# Revit family: Planting_-_Solid_and_RPC_16077
name_source: partatom
category: Planting
revit_build: Autodesk Revit Architecture 2015 (Build: 20140322_1515(x64)
units: mm (PartAtom-declared; Revit-internal decimal feet)

## types (15) — shared parameters
Assembly Code = G2050500
Planting Profile Material = <By Category>

## per-type parameters (varying)
| type | Canopy Height | Canopy Ratio | Form | Height | Reference Plane Height | Truck Width | Width |
| Deciduous - Med - Ash | 28' - 8 13/32" | 0.82 | Solids : Round Upright | 35' - 0" | 17' - 6" | 1' - 8" | 25' - 0" |
| Deciduous - Large - Oak, Skinny | 42' - 0" | 0.84 | Solids : Round | 50' - 0" | 25' - 0" | 2' - 8" | 40' - 0" |
| Deciduous - Large - Oak, Wide | 46' - 2 13/32" | 0.84 | Solids : Round | 55' - 0" | 27' - 6" | 3' - 1 19/32" | 47' - 0" |
| Deciduous - Med - Honey Locust | 34' - 4 13/16" | 0.86 | Solids : Vase | 40' - 0" | 20' - 0" | 1' - 8" | 25' - 0" |
| Deciduous - Large - Beech | 37' - 4 3/16" | 0.83 | Solids : Round | 45' - 0" | 22' - 6" | 2' - 3 3/16" | 34' - 0" |
| Deciduous - Small - Serviceberry | 22' - 6" | 0.9 | Solids : Round | 25' - 0" | 12' - 6" | 1' - 0" | 15' - 0" |
| Deciduous - Med - Birch | 27' - 0" | 0.9 | Solids : Round Upright | 30' - 0" | 15' - 0" | 1' - 0" | 15' - 0" |
| Evergreen - Juniper, Wide | 24' - 6" | 0.98 | Solids : Columnar | 25' - 0" | 12' - 6" | 0' - 8" | 10' - 0" |
| Evergreen - Juniper, Skinny | 34' - 3 19/32" | 0.98 | Solids : Columnar | 35' - 0" | 17' - 6" | 0' - 6 13/32" | 8' - 0" |
| Evergreen - Fir | 31' - 6" | 0.9 | Solids : Conical | 35' - 0" | 17' - 6" | 1' - 4" | 20' - 0" |
| Evergreen - Hemlock | 33' - 3" | 0.95 | Solids : Pyramidal | 35' - 0" | 17' - 6" | 1' - 2 13/32" | 18' - 0" |
| Evergreen - Spruce | 42' - 3 19/32" | 0.94 | Solids : Conical | 45' - 0" | 22' - 6" | 1' - 4" | 20' - 0" |
| Deciduous - Small - Blueberry | 20' - 0" | 0.8 | Solids : Vase | 25' - 0" | 12' - 6" | 1' - 8" | 25' - 0" |
| Deciduous - Small - Cherry | 24' - 7 3/16" | 0.82 | Solids : Vase | 30' - 0" | 15' - 0" | 1' - 2 13/32" | 18' - 0" |
| Deciduous - Small - Apple | 24' - 0" | 0.8 | Solids : Vase | 30' - 0" | 15' - 0" | 2' - 1 19/32" | 32' - 0" |

## geometry (parser evidence)
native form markers: Sweep x2
no freeform markers — native parametric forms only
